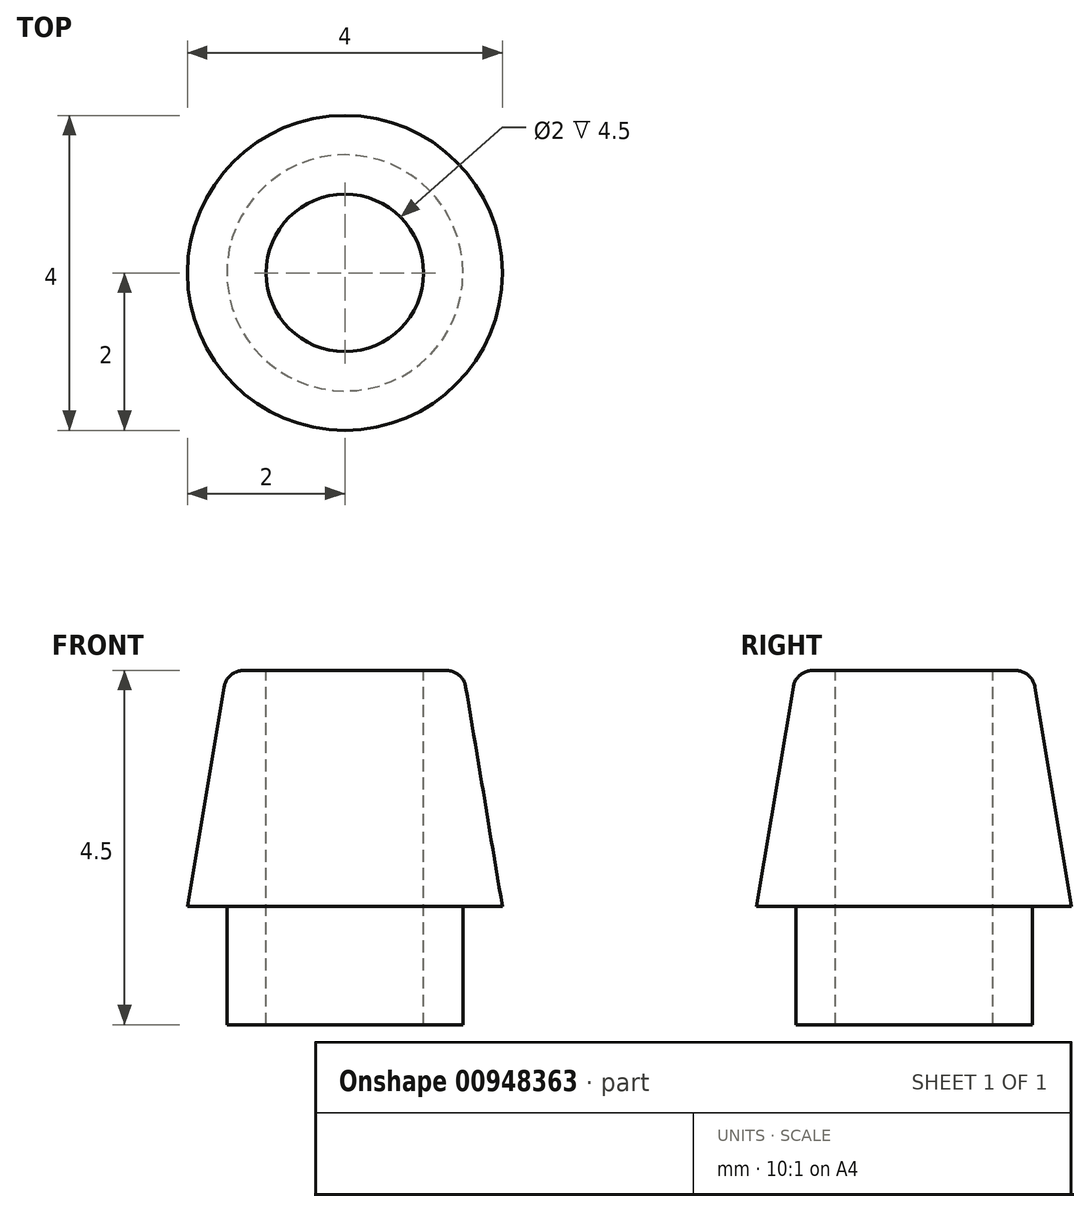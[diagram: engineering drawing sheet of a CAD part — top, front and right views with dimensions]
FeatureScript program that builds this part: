
annotation { "Feature Type Name" : "Feature", "Feature Type Description" : "" }
export const myFeature = defineFeature(function(context is Context, id is Id, definition is map)
    precondition{}
    {
        {
            var Q0;
            Q0=qCreatedBy(makeId("Front.planeOp"),FACE);
            var sketch = newSketch(context, id + "F0", { "sketchPlane" : qUnion([Q0])});
            skLineSegment(sketch, "E0", {"start": v(0, 0) * mm, "end": v(2, 0) * mm});
            skLineSegment(sketch, "E1", {"start": v(2, 0) * mm, "end": v(1.5, 3) * mm});
            skLineSegment(sketch, "E2", {"start": v(1.5, 3) * mm, "end": v(0, 3) * mm});
            skLineSegment(sketch, "E3", {"start": v(0, 3) * mm, "end": v(0, 0) * mm});
            skLineSegment(sketch, "E4", {"start": v(1.5, 0) * mm, "end": v(1.5, -1.5) * mm});
            skLineSegment(sketch, "E5", {"start": v(1.5, -1.5) * mm, "end": v(0, -1.5) * mm});
            skLineSegment(sketch, "E6", {"start": v(0, -1.5) * mm, "end": v(0, 0) * mm});
            skSolve(sketch);
        }
        {
            var Q0;
            Q0 = qSketchRegion(id + "F0", true);
            var Q1;
            Q1=sQuery(id+"F0.wireOp",EDGE,"E3");
            revolve(context, id + "F1", {"surfaceOperationType" : NewSurfaceOperationType.NEW, "entities" : qUnion([Q0]), "axis" : qUnion([Q1]), "revolveType" : RevolveType.FULL});
        }
        {
            var Q0;
            Q0=makeQuery(id+"F1.opRevolve","SWEPT_FACE",FACE,{"disambiguationData":[OSD([sQuery(id+"F0.wireOp",EDGE,"E2")])]});
            var sketch = newSketch(context, id + "F2", { "sketchPlane" : qUnion([Q0])});
            skCircle(sketch, "E7", {"center": v(0, 0) * mm, "radius": 1 * mm});
            skSolve(sketch);
        }
        {
            var Q0;
            Q0 = qSketchRegion(id + "F2", true);
            extrude(context, id + "F3", {"entities" : qUnion([Q0]), "operationType" : NewBodyOperationType.REMOVE, "oppositeDirection" : true, "depth" : 25 * mm, "offsetDistance" : 25 * mm});
        }
        {
            var Q0;
            Q0=makeQuery(id+"F1.opRevolve","SWEPT_EDGE",EDGE,{"disambiguationData":[OSD([sQuery(id+"F0.wireOp",EDGE,"E1"),sQuery(id+"F0.wireOp",EDGE,"E2")])]});
            fillet(context, id + "F4", {"entities" : qUnion([Q0]), "radius" : 0.25 * mm, "tangentPropagation" : true, "allowEdgeOverflow" : false});
        }
    });
